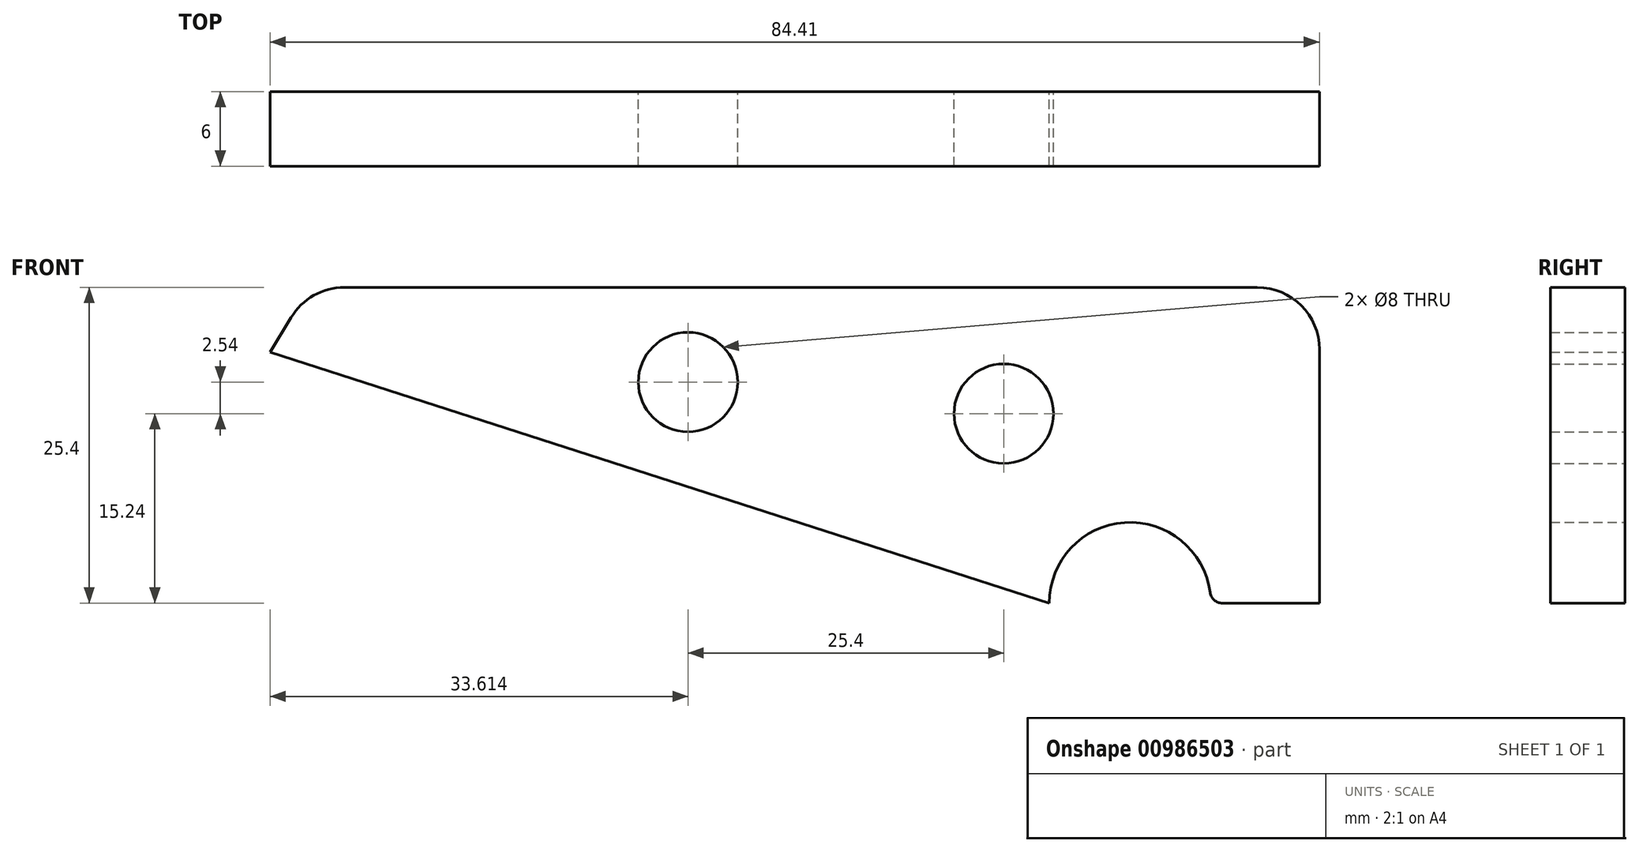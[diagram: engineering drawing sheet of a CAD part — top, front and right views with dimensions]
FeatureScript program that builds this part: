
annotation { "Feature Type Name" : "Feature", "Feature Type Description" : "" }
export const myFeature = defineFeature(function(context is Context, id is Id, definition is map)
    precondition{}
    {
        {
            var Q0;
            Q0=qCreatedBy(makeId("Front.planeOp"),FACE);
            var sketch = newSketch(context, id + "F0", { "sketchPlane" : qUnion([Q0])});
            skLineSegment(sketch, "E0", {"start": v(-40.67, 0) * mm, "end": v(40.61, 0) * mm});
            skLineSegment(sketch, "E1", {"start": v(40.61, 0) * mm, "end": v(40.61, -25.4) * mm});
            skLineSegment(sketch, "E2", {"start": v(40.61, -25.4) * mm, "end": v(35.37, -25.4) * mm});
            skLineSegment(sketch, "E3", {"start": v(40.61, 0) * mm, "end": v(40.61, -6.35) * mm});
            skLineSegment(sketch, "E4", {"start": v(-40.67, 0) * mm, "end": v(-43.8, -5.23) * mm});
            skLineSegment(sketch, "E5", {"start": v(40.61, 0) * mm, "end": v(40.61, -10.16) * mm});
            skCircle(sketch, "E6", {"center": v(15.21, -10.16) * mm, "radius": 4 * mm});
            skLineSegment(sketch, "E7", {"start": v(40.61, 0) * mm, "end": v(40.61, -7.62) * mm});
            skCircle(sketch, "E8", {"center": v(-10.19, -7.62) * mm, "radius": 4 * mm});
            skLineSegment(sketch, "E9", {"start": v(40.61, -25.4) * mm, "end": v(31.87, -25.4) * mm});
            skArc(sketch, "E10", {"start": v(31.87, -25.4) * mm, "mid": v(25.37, -18.9) * mm, "end": v(18.87, -25.4) * mm});
            skLineSegment(sketch, "E11", {"start": v(18.87, -25.4) * mm, "end": v(-43.8, -5.23) * mm});
            skSolve(sketch);
        }
        {
            var Q0;
            Q0 = qSketchRegion(id + "F0", true);
            extrude(context, id + "F1", {"entities" : qUnion([Q0]), "depth" : 6 * mm, "offsetDistance" : 25 * mm});
        }
        {
            var Q0;
            Q0=makeQuery(id+"F1.opExtrude","SWEPT_EDGE",EDGE,{"disambiguationData":[OSD([sQuery(id+"F0.wireOp",EDGE,"E0"),sQuery(id+"F0.wireOp",EDGE,"E7")])]});
            fillet(context, id + "F2", {"entities" : qUnion([Q0]), "radius" : 5 * mm, "tangentPropagation" : true, "allowEdgeOverflow" : false});
        }
        {
            var Q0;
            Q0=makeQuery(id+"F1.opExtrude","SWEPT_EDGE",EDGE,{"disambiguationData":[OSD([sQuery(id+"F0.wireOp",EDGE,"E9"),sQuery(id+"F0.wireOp",EDGE,"E10")])]});
            fillet(context, id + "F3", {"entities" : qUnion([Q0]), "radius" : 1 * mm, "tangentPropagation" : true, "allowEdgeOverflow" : false});
        }
    });
